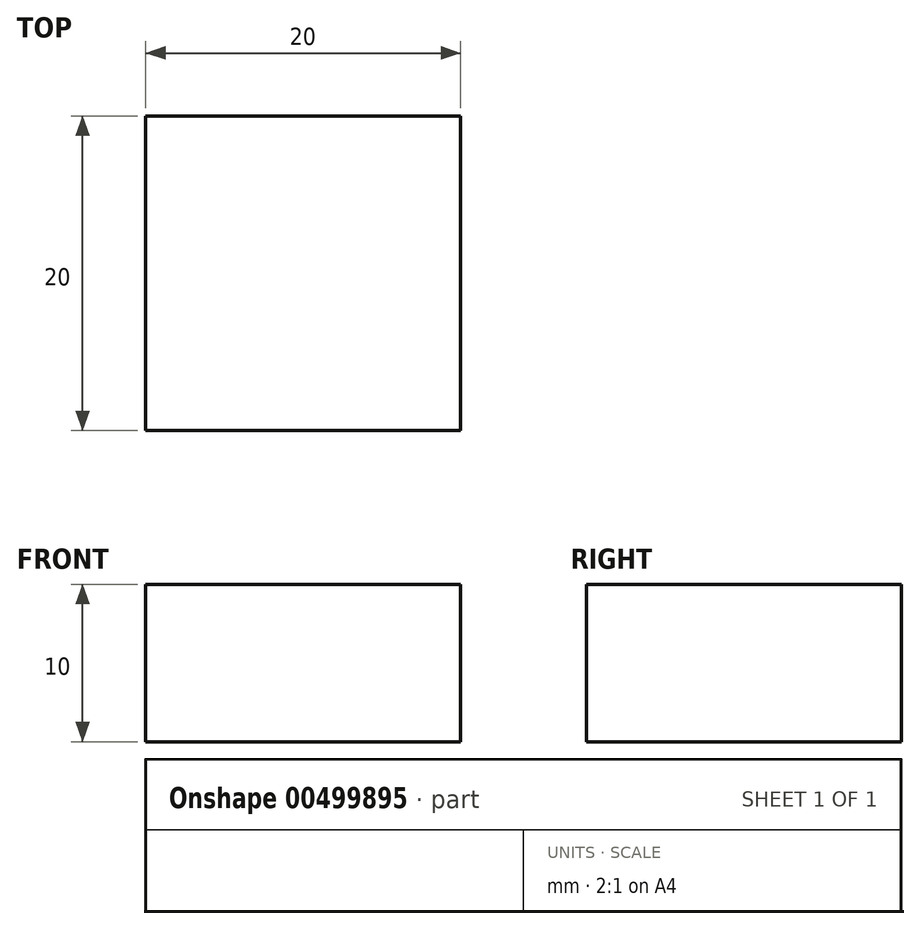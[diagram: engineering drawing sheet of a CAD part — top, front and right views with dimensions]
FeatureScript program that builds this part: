
annotation { "Feature Type Name" : "Feature", "Feature Type Description" : "" }
export const myFeature = defineFeature(function(context is Context, id is Id, definition is map)
    precondition{}
    {
        {
            var Q0;
            Q0=qCreatedBy(makeId("Top.planeOp"),FACE);
            var sketch = newSketch(context, id + "F0", { "sketchPlane" : qUnion([Q0])});
            skLineSegment(sketch, "E0.bottom", {"start": v(-32.51, 37.34) * mm, "end": v(-12.51, 37.34) * mm});
            skLineSegment(sketch, "E0.top", {"start": v(-32.51, 17.34) * mm, "end": v(-12.51, 17.34) * mm});
            skLineSegment(sketch, "E0.left", {"start": v(-32.51, 37.34) * mm, "end": v(-32.51, 17.34) * mm});
            skLineSegment(sketch, "E0.right", {"start": v(-12.51, 37.34) * mm, "end": v(-12.51, 17.34) * mm});
            skSolve(sketch);
        }
        {
            var Q0;
            Q0 = qSketchRegion(id + "F0", true);
            extrude(context, id + "F1", {"entities" : qUnion([Q0]), "depth" : 10 * mm});
        }
    });
